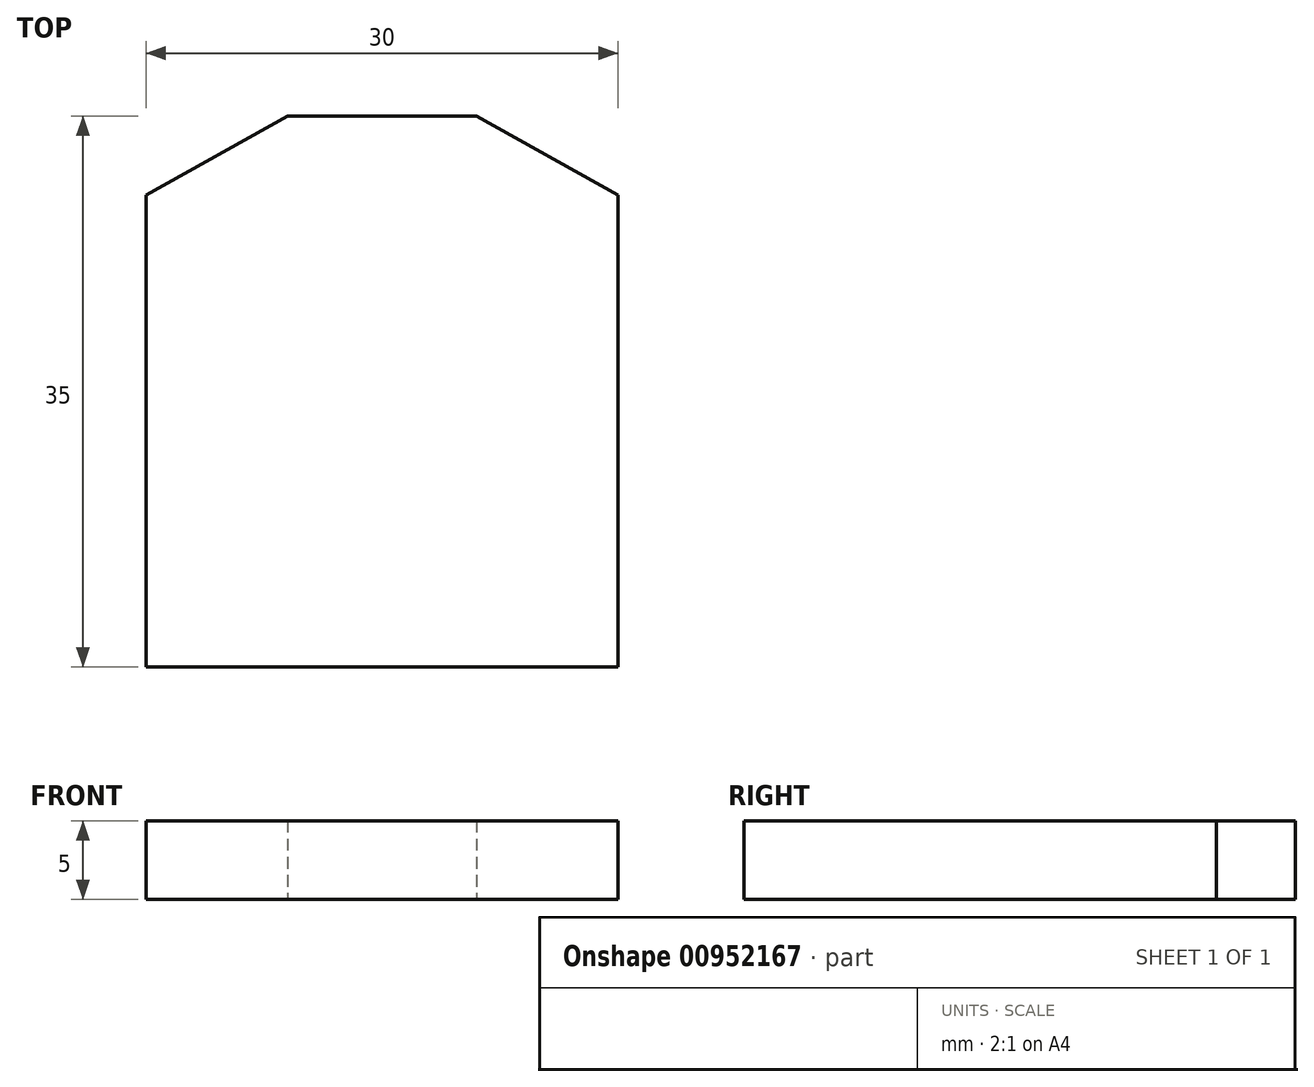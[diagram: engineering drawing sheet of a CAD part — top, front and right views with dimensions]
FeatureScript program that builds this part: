
annotation { "Feature Type Name" : "Feature", "Feature Type Description" : "" }
export const myFeature = defineFeature(function(context is Context, id is Id, definition is map)
    precondition{}
    {
        {
            var Q0;
            Q0=qCreatedBy(makeId("Top.planeOp"),FACE);
            var sketch = newSketch(context, id + "F0", { "sketchPlane" : qUnion([Q0])});
            skLineSegment(sketch, "E0.bottom", {"start": v(-15, 0) * mm, "end": v(15, 0) * mm});
            skLineSegment(sketch, "E0.left", {"start": v(-15, 0) * mm, "end": v(-15, 30) * mm});
            skLineSegment(sketch, "E0.right", {"start": v(15, 0) * mm, "end": v(15, 30) * mm});
            skLineSegment(sketch, "E1", {"start": v(-15, 30) * mm, "end": v(-6, 35) * mm});
            skLineSegment(sketch, "E2", {"start": v(-6, 35) * mm, "end": v(6, 35) * mm});
            skLineSegment(sketch, "E3", {"start": v(6, 35) * mm, "end": v(15, 30) * mm});
            skSolve(sketch);
        }
        {
            var Q0;
            Q0=makeQuery(id+"F0.imprint","IMPRINT",FACE,{"disambiguationData":[TD([[makeQuery(id+"F0.imprint","IMPRINT",EDGE,{"derivedFrom":sQuery(id+"F0.wireOp",EDGE,"E0.bottom")}),1.0]])]});
            extrude(context, id + "F1", {"entities" : qUnion([Q0]), "depth" : 5 * mm, "offsetDistance" : 25 * mm});
        }
    });
